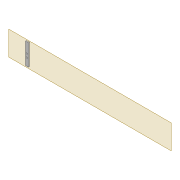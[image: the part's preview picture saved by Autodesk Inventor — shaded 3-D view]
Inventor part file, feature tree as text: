
AUTODESK INVENTOR PART (.ipt)
format: ipt  version: 2022 (Build 260153000, 153)  size: 432,640 bytes
history: native  units: mm
features: sketch x8, projected_geometry x8, extrude x7, shell x1, plane x1, chamfer x1
ambient origin geometry x8: Origin, YZ Plane, XZ Plane, XY Plane, X Axis, Y Axis, Z Axis, Center Point
bodies: Solid1 (feature_tree)
feature tree (26):
  extrude  "Extrusion1"  Depth=2.0mm
  shell  "Shell1"  Thickness=2.0mm
  extrude  "Extrusion8"  Depth=2.0mm
  extrude  "Extrusion3"  Depth=10.0mm TaperAngle=0.0deg
  extrude  "Extrusion4"  Depth=5.0mm
  extrude  "Extrusion5"  Depth=2.5mm
  plane  "Work Plane2"
  extrude  "Extrusion9"  Depth=5.0mm
  chamfer  "Chamfer1"  Distance=5.0mm
  extrude  "Extrusion11"  Depth=2.0mm TaperAngle=0.0deg
  sketch  "Sketch32"  dims[d62=67.0mm d63=5.0mm d64=2.0mm d65=0.0mm d66=2.5mm d67=12.0mm d68=75.0mm d69=20.0mm d70=0.5mm d71=10.0mm d72=0.0mm d75=3.0mm d76=3.0mm d77=2.0mm d78=45.0deg d79=0.0mm d80=1.0mm d81=1.0mm d82=1.0mm d83=1.0mm d84=1.0mm d85=10.0mm d86=0.0mm]
  sketch  "Sketch30"  dims[d40=2.5mm]
  sketch  "Sketch3"  dims[d0=2.0mm d1=0.0mm d2=4.0mm d7=2.0mm]
  sketch  "Sketch8"  dims[d8=2.0mm d9=5.9mm]
  sketch  "Sketch9"  dims[d13=10.0mm d14=0.0mm d16=10.0mm d17=0.0mm]
  projected_geometry  "Projected Loop4"
  projected_geometry  "Projected Loop10"
  sketch  "Sketch24"  dims[d22=2.0mm d23=0.0mm d32=5.0mm]
  projected_geometry  "Projected Loop11"
  projected_geometry  "Projected Loop12"
  sketch  "Sketch26"  dims[d34=1.6mm d35=2.5mm]
  projected_geometry  "Projected Loop13"
  sketch  "Sketch28"  dims[d37=5.0mm d38=1.6mm]
  projected_geometry  "Project Cut Edges1"
  projected_geometry  "Project Cut Edges3"
  projected_geometry  "Project Cut Edges4"
